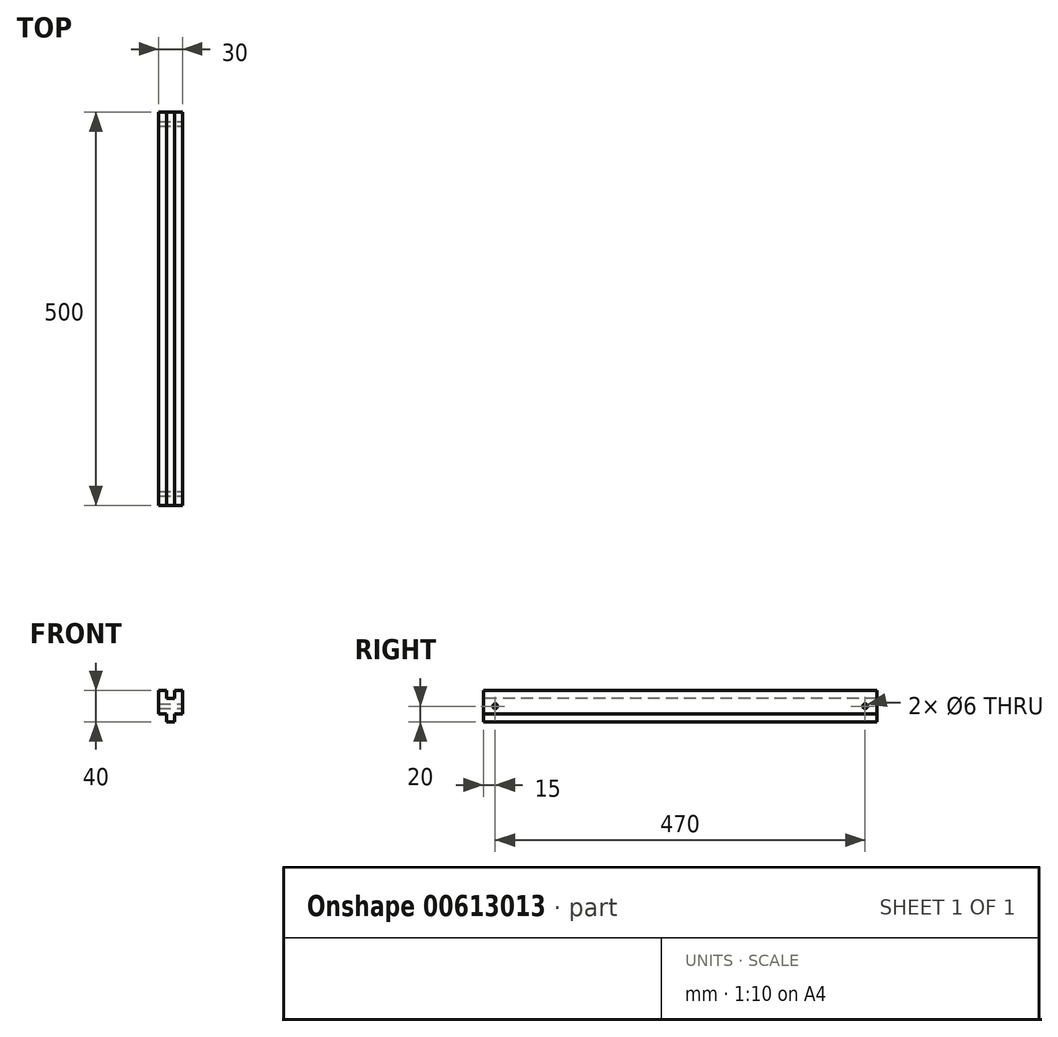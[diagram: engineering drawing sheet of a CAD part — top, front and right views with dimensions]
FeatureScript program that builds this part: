
annotation { "Feature Type Name" : "Feature", "Feature Type Description" : "" }
export const myFeature = defineFeature(function(context is Context, id is Id, definition is map)
    precondition{}
    {
        {
            var Q0;
            Q0=qCreatedBy(makeId("Right.planeOp"),FACE);
            var sketch = newSketch(context, id + "F0", { "sketchPlane" : qUnion([Q0])});
            skLineSegment(sketch, "E0.bottom", {"start": v(250, -10) * mm, "end": v(-250, -10) * mm});
            skLineSegment(sketch, "E0.top", {"start": v(250, 10) * mm, "end": v(-250, 10) * mm});
            skLineSegment(sketch, "E0.left", {"start": v(250, -10) * mm, "end": v(250, 10) * mm});
            skLineSegment(sketch, "E0.right", {"start": v(-250, -10) * mm, "end": v(-250, 10) * mm});
            skPoint(sketch, "E0.middle", {"position": v(0, 0) * mm});
            skSolve(sketch);
        }
        {
            var Q0;
            Q0=qSketchRegion(id+"F0",true);
            extrude(context, id + "F1", {"entities" : qUnion([Q0]), "depth" : 30 * mm, "offsetDistance" : 25 * mm});
        }
        {
            var Q0;
            Q0=makeQuery(id+"F1.opExtrude","SWEPT_FACE",FACE,{"disambiguationData":[OSD([sQuery(id+"F0.wireOp",EDGE,"E0.right")])]});
            var sketch = newSketch(context, id + "F2", { "sketchPlane" : qUnion([Q0])});
            skLineSegment(sketch, "E1.bottom", {"start": v(10, 10) * mm, "end": v(0, 10) * mm});
            skLineSegment(sketch, "E1.top", {"start": v(10, 20) * mm, "end": v(0, 20) * mm});
            skLineSegment(sketch, "E1.left", {"start": v(10, 10) * mm, "end": v(10, 20) * mm});
            skLineSegment(sketch, "E1.right", {"start": v(0, 10) * mm, "end": v(0, 20) * mm});
            skPoint(sketch, "E1.middle", {"position": v(5, 15) * mm});
            skSolve(sketch);
        }
        {
            var Q0;
            Q0=qSketchRegion(id+"F2",true);
            extrude(context, id + "F3", {"entities" : qUnion([Q0]), "operationType" : NewBodyOperationType.ADD, "depth" : -500 * mm, "offsetDistance" : 25 * mm});
        }
        {
            var Q0;
            Q0=makeQuery(id+"F3.boolean.opBoolean","MERGE",FACE,{"derivedFrom":[makeQuery(id+"F1.opExtrude","SWEPT_FACE",FACE,{"disambiguationData":[OSD([sQuery(id+"F0.wireOp",EDGE,"E0.right")])]}),makeQuery(id+"F3.opExtrude","CAP_FACE",FACE,{"disambiguationData":[OSD([sQuery(id+"F2.wireOp",EDGE,"E1.bottom"),sQuery(id+"F2.wireOp",EDGE,"E1.top"),sQuery(id+"F2.wireOp",EDGE,"E1.left"),sQuery(id+"F2.wireOp",EDGE,"E1.right")])],"isStart":true})]});
            var sketch = newSketch(context, id + "F4", { "sketchPlane" : qUnion([Q0])});
            skLineSegment(sketch, "E2.bottom", {"start": v(30, 10) * mm, "end": v(20, 10) * mm});
            skLineSegment(sketch, "E2.top", {"start": v(30, 20) * mm, "end": v(20, 20) * mm});
            skLineSegment(sketch, "E2.left", {"start": v(30, 10) * mm, "end": v(30, 20) * mm});
            skLineSegment(sketch, "E2.right", {"start": v(20, 10) * mm, "end": v(20, 20) * mm});
            skPoint(sketch, "E2.middle", {"position": v(25, 15) * mm});
            skSolve(sketch);
        }
        {
            var Q0;
            Q0=qSketchRegion(id+"F4",true);
            extrude(context, id + "F5", {"entities" : qUnion([Q0]), "operationType" : NewBodyOperationType.ADD, "depth" : -500 * mm, "offsetDistance" : 25 * mm});
        }
        {
            var Q0;
            Q0=makeQuery(id+"F5.boolean.opBoolean","MERGE",FACE,{"derivedFrom":[makeQuery(id+"F3.boolean.opBoolean","MERGE",FACE,{"derivedFrom":[makeQuery(id+"F1.opExtrude","SWEPT_FACE",FACE,{"disambiguationData":[OSD([sQuery(id+"F0.wireOp",EDGE,"E0.right")])]}),makeQuery(id+"F3.opExtrude","CAP_FACE",FACE,{"disambiguationData":[OSD([sQuery(id+"F2.wireOp",EDGE,"E1.bottom"),sQuery(id+"F2.wireOp",EDGE,"E1.top"),sQuery(id+"F2.wireOp",EDGE,"E1.left"),sQuery(id+"F2.wireOp",EDGE,"E1.right")])],"isStart":true})]}),makeQuery(id+"F5.opExtrude","CAP_FACE",FACE,{"disambiguationData":[OSD([sQuery(id+"F4.wireOp",EDGE,"E2.bottom"),sQuery(id+"F4.wireOp",EDGE,"E2.top"),sQuery(id+"F4.wireOp",EDGE,"E2.left"),sQuery(id+"F4.wireOp",EDGE,"E2.right")])],"isStart":true})]});
            var sketch = newSketch(context, id + "F6", { "sketchPlane" : qUnion([Q0])});
            skLineSegment(sketch, "E3.bottom", {"start": v(20, -20) * mm, "end": v(10, -20) * mm});
            skLineSegment(sketch, "E3.top", {"start": v(20, -10) * mm, "end": v(10, -10) * mm});
            skLineSegment(sketch, "E3.left", {"start": v(20, -20) * mm, "end": v(20, -10) * mm});
            skLineSegment(sketch, "E3.right", {"start": v(10, -20) * mm, "end": v(10, -10) * mm});
            skPoint(sketch, "E3.middle", {"position": v(15, -15) * mm});
            skSolve(sketch);
        }
        {
            var Q0;
            Q0 = qSketchRegion(id + "F6", true);
            extrude(context, id + "F7", {"entities" : qUnion([Q0]), "operationType" : NewBodyOperationType.ADD, "depth" : -500 * mm, "offsetDistance" : 25 * mm});
        }
        {
            var Q0;
            Q0=makeQuery(id+"F5.boolean.opBoolean","MERGE",FACE,{"derivedFrom":[makeQuery(id+"F1.opExtrude","CAP_FACE",FACE,{"disambiguationData":[OSD([sQuery(id+"F0.wireOp",EDGE,"E0.bottom"),sQuery(id+"F0.wireOp",EDGE,"E0.top"),sQuery(id+"F0.wireOp",EDGE,"E0.left"),sQuery(id+"F0.wireOp",EDGE,"E0.right")])],"isStart":false}),makeQuery(id+"F5.opExtrude","SWEPT_FACE",FACE,{"disambiguationData":[OSD([sQuery(id+"F4.wireOp",EDGE,"E2.left")])]})]});
            var sketch = newSketch(context, id + "F8", { "sketchPlane" : qUnion([Q0])});
            skCircle(sketch, "E4", {"center": v(-235, 0) * mm, "radius": 3 * mm});
            skCircle(sketch, "E5", {"center": v(235, 0) * mm, "radius": 3 * mm});
            skSolve(sketch);
        }
        {
            var Q0;
            Q0 = qSketchRegion(id + "F8", true);
            extrude(context, id + "F9", {"entities" : qUnion([Q0]), "operationType" : NewBodyOperationType.REMOVE, "oppositeDirection" : true, "depth" : 30 * mm, "offsetDistance" : 25 * mm});
        }
    });
